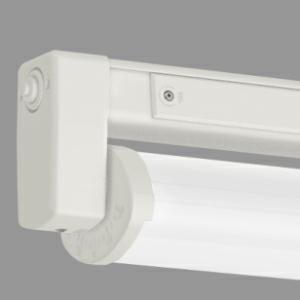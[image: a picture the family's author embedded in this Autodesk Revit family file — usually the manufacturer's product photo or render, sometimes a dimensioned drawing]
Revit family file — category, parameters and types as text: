
# Revit family: erfurt_led_extreme_m1200_-_4030lm___pmma_transopal_r___schlagzah__840_4000k__raumstrahlend_4334803421_2d7e
name_source: partatom
category: Lighting Fixtures
units: mm (PartAtom-declared; Revit-internal decimal feet)

## family parameters
Cut with Voids When Loaded = No
Host = Face
Light Source = No
Part Type = Normal
Room Calculation Point = No
Round Connector Dimension = Use Diameter
Shared = No

## types (1)
- ERFURT LED EXTREME m1200 - 4030lm , PMMA Transopal® (schlagzäh), 840/4000K, raumstrahlend (1 x LED Stripe, 4030 lm, 25 W, 840/4000K)
    Apparent Load = 28 VA
    Approval mark = CE, ENEC
    CIE Flux Codes = 56 85 96 98 98
    Color Rendering = 1B/80..89
    Color Temperature = 840/4000K
    Default Elevation = 1800 mm
    Description = Polymer luminaire for surface ceiling mounting with LED lamps, single or twin lamps. Useable in industrial applications and areas with special safety requirements. Long expected service life, useable up to +65 °C. Weather-proof and UV-resistant luminaire housing made of fibreglass-reinforced polymer, similar to RAL 9010. Useable for indoor and outdoor areas according to protection rating IP 65 (single or twin lamp). Thermally separated lamp chamber and driver chamber. Short sealing system consisting of age-resistant, form-retaining silicone/ synthetic rubber. Reflector tube with sealing system for easy LED replacement (easy eXchange LED). With reflector tubes that can be swivelled independently made of PMMA Transopal® (impact strengthened) or PC Tropal® (fracture proof) with internal aluminium reflector (MIRO-SILVER®). Reflector tube can be locked in increments of 10°. Luminaire ready for mounting and installation. Built-in driver 230 V AC/DC. Two cable entries M20 on face side and 4 x 1.5 mm² through wiring. Two access covers. L80 B10 > 100,000 h at +65 °C. 4 kV transient filter. 8 years manufacturer warranty. Single or row mounting. Ceiling or wall fixing using two stainless steel mounting clamps with variable mounting distance.


Length: 1251 mm
Width: 107 mm
Height: 140 mm
Weight: 2.8 kg

LOR: 97.7 %
    Height = 140 mm  [stored 0.459318 ft]
    Lamp = 1 x LED Stripe
    Lamp Light Flux = 4030 lm
    Lamp Power = 25 W
    Lamp count = 1
    Length = 1251 mm
    Lifetime = 100000 h
    Luminous efficacy = 141 lm/W
    Manufacturer = NORKA
    ModVariant = No
    Model = 4334803421
    Mounting Place = Ceiling, Wall
    Mounting Type = Surface mounted, Rail mounted
    Number of Poles = 1
    OnlyDefault = Yes
    Power Factor = 1
    Product Name = ERFURT LED EXTREME m1200 - 4030lm , PMMA Transopal® (schlagzäh), 840/4000K, raumstrahlend
    Product group = Ceiling-/wall luminaire
    ProductGroupID = 30
    Protection Class = Protection class II
    Protection Degree = IP 65
    RLX_Detail_Level = 1
    RlxData = <blob elided: 160381 chars, md5=71cd4e8a>
    Socket = socket
    Standby Power = 0 W
    System Light Flux = 3937 lm
    System Power = 28 W
    Type Comments = Product without accessories
    Type Image = erfurt-led-transopal.jpg
    URL = http://relux.com
    VarID = ---
    Voltage = 0 V
    Weight = 0.00 kg
    Width = 107 mm

note: [stored X ft] marks values corroborated as IEEE doubles in the binary element streams (Revit-internal decimal feet)

## geometry (parser evidence)
native form markers: Blend x4, Sweep x13
no freeform markers — native parametric forms only
